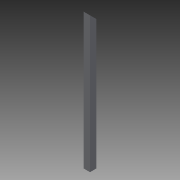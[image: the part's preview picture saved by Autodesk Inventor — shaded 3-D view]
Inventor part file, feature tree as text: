
AUTODESK INVENTOR PART (.ipt)
format: ipt  version: 2013 (Build 170138000, 138)  size: 82,432 bytes
history: native  units: in
note: dims shown in document units (in); Inventor stores cm internally (conversion verified against a paired STEP export)
features: extrude x2, sketch x2
ambient origin geometry x8: Origin, YZ Plane, XZ Plane, XY Plane, X Axis, Y Axis, Z Axis, Center Point
bodies: Solid1 (feature_tree)
feature tree (4):
  extrude  "Extrusion1"  Depth=1.0in
  extrude  "Extrusion2"  Depth=0.75in
  sketch  "Sketch1"  dims[d0=1.0in d1=1.0in]
  sketch  "Sketch2"  dims[d2=0.75in d3=0.75in d4=21.0in d5=0.0in d6=45.0deg d7=1.0in d8=0.0in]
